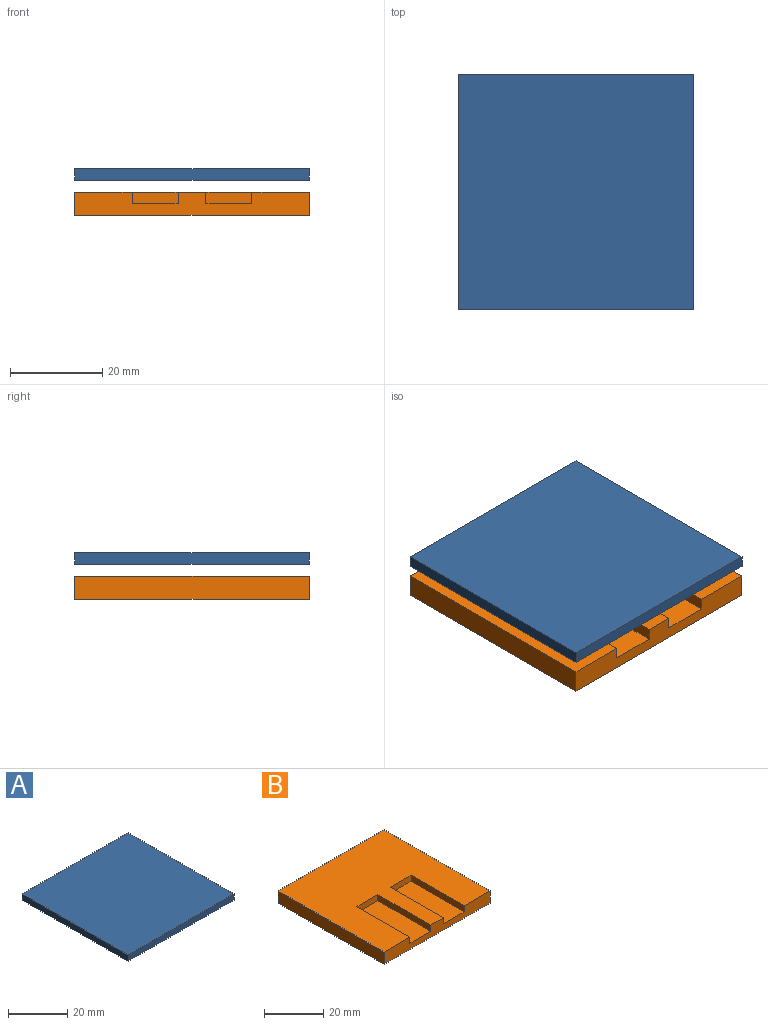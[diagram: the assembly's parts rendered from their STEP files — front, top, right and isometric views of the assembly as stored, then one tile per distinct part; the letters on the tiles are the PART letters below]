
ASSEMBLY  parts=2 mates=2
PART A: 6 faces, bbox 50.8x50.8x2.5 mm
  f0: plane 50.8x2.54mm, normal (0,1,0), area 129mm2, adj f1,f3,f4,f5
  f1: plane 50.8x2.54mm, normal (-1,0,0), area 129mm2, adj f0,f2,f4,f5
  f2: plane 50.8x2.54mm, normal (0,-1,0), area 129mm2, adj f1,f3,f4,f5
  f3: plane 50.8x2.54mm, normal (1,0,0), area 129mm2, adj f0,f2,f4,f5
  f4: plane 50.8x50.8mm, normal (0,0,1), area 2580.6mm2, adj f0,f1,f2,f3
  f5: plane 50.8x50.8mm, normal (0,0,-1), area 2580.6mm2, adj f0,f1,f2,f3
PART B: 14 faces, bbox 50.8x50.8x5.1 mm
  f0: plane 25.4x9.95mm, normal (0,0,1), area 252.7mm2, adj f4,f10,f11,f12
  f1: plane 25.4x9.95mm, normal (0,0,1), area 252.7mm2, adj f4,f7,f8,f9
  f2: plane 50.8x5.08mm, normal (0,1,0), area 258.1mm2, adj f3,f5,f6,f13
  f3: plane 50.8x5.08mm, normal (-1,0,0), area 258.1mm2, adj f2,f4,f6,f13
  f4: plane 50.8x5.08mm, normal (0,-1,0), area 207.5mm2, adj f0,f1,f3,f5,f6,f7,f9,f10
  f5: plane 50.8x5.08mm, normal (1,0,0), area 258.1mm2, adj f2,f4,f6,f13
  f6: plane 50.8x50.8mm, normal (0,0,-1), area 2580.6mm2, adj f2,f3,f4,f5
  f7: plane 25.4x2.54mm, normal (1,0,0), area 64.5mm2, adj f1,f4,f8,f13
  f8: plane 9.95x2.54mm, normal (0,-1,0), area 25.3mm2, adj f1,f7,f9,f13
  f9: plane 25.4x2.54mm, normal (-1,0,0), area 64.5mm2, adj f1,f4,f8,f13
  f10: plane 25.4x2.54mm, normal (1,0,0), area 64.5mm2, adj f0,f4,f11,f13
  f11: plane 9.95x2.54mm, normal (0,-1,0), area 25.3mm2, adj f0,f10,f12,f13
  f12: plane 25.4x2.54mm, normal (-1,0,0), area 64.5mm2, adj f0,f4,f11,f13
  f13: plane 50.8x50.8mm, normal (0,0,1), area 2075.2mm2, adj f2,f3,f4,f5,f7,f8,f9,f10
PLACE A t=(11.03,-35.79,7.61)mm
PLACE B t=(-68.22,-43.67,-0.01)mm
MATE planar A.f3 <-> B.f5  axis (1,0,0) through (11.03,10.82,7.61)mm
MATE planar A.f1 <-> B.f3  axis (-1,0,0) through (-39.77,10.82,7.61)mm
